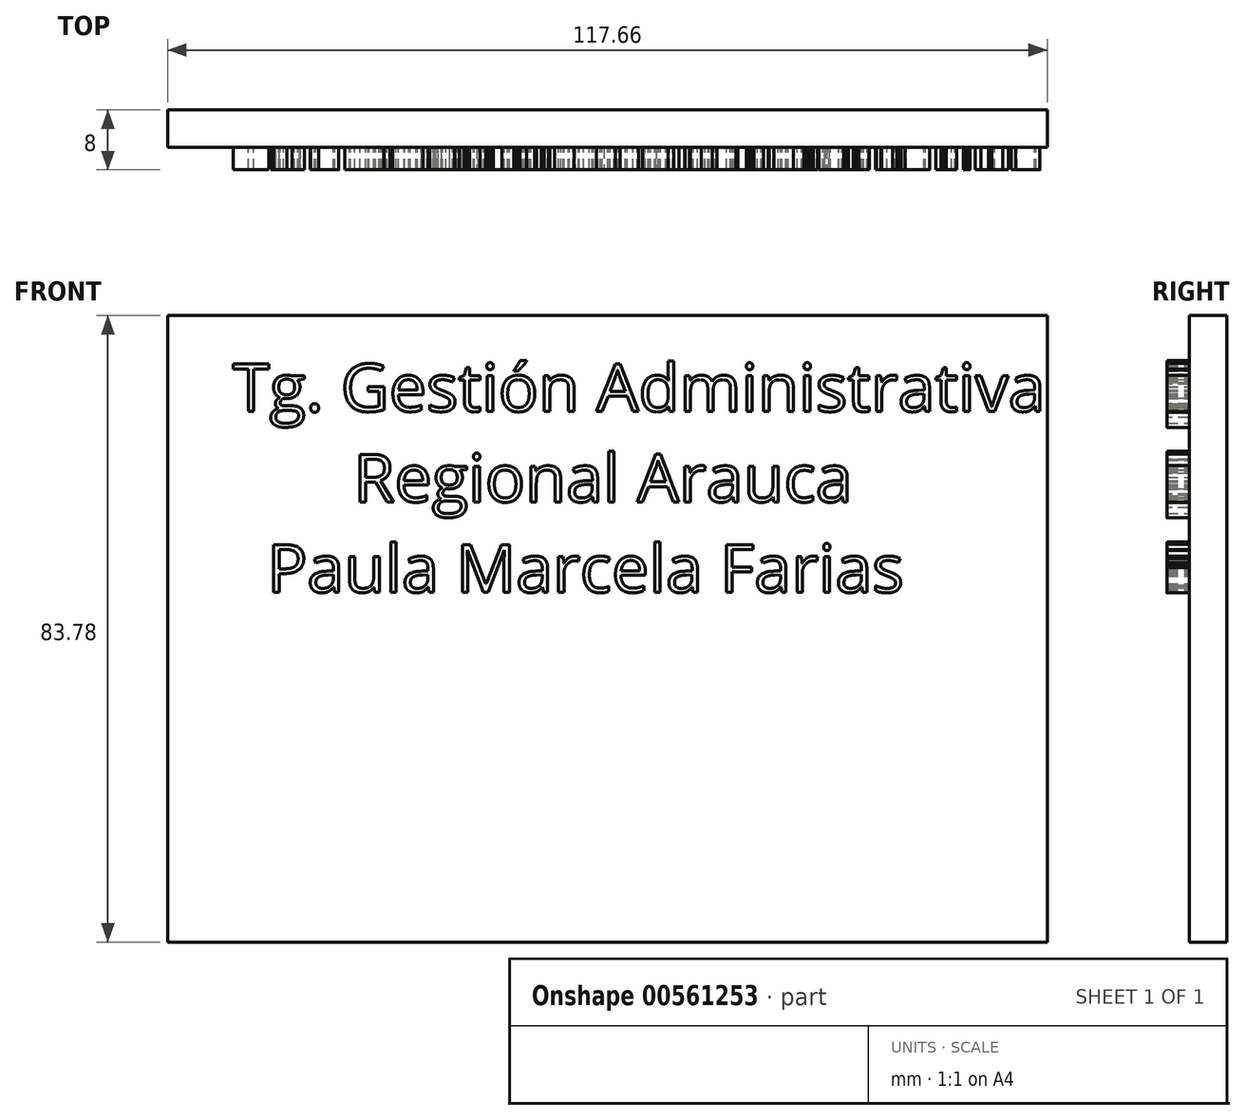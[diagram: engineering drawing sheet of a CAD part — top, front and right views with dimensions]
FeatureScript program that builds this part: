
annotation { "Feature Type Name" : "Feature", "Feature Type Description" : "" }
export const myFeature = defineFeature(function(context is Context, id is Id, definition is map)
    precondition{}
    {
        {
            var Q0;
            Q0=qCreatedBy(makeId("Front.planeOp"),FACE);
            var sketch = newSketch(context, id + "F0", { "sketchPlane" : qUnion([Q0])});
            skLineSegment(sketch, "E0.bottom", {"start": v(58.83, 41.9) * mm, "end": v(-58.83, 41.9) * mm});
            skLineSegment(sketch, "E0.top", {"start": v(58.83, -41.9) * mm, "end": v(-58.83, -41.9) * mm});
            skLineSegment(sketch, "E0.left", {"start": v(58.83, 41.9) * mm, "end": v(58.83, -41.9) * mm});
            skLineSegment(sketch, "E0.right", {"start": v(-58.83, 41.9) * mm, "end": v(-58.83, -41.9) * mm});
            skPoint(sketch, "E0.middle", {"position": v(0, 0) * mm});
            skSolve(sketch);
        }
        {
            var Q0;
            Q0=makeQuery(id+"F0.imprint","IMPRINT",FACE,{"disambiguationData":[TD([[makeQuery(id+"F0.imprint","IMPRINT",EDGE,{"derivedFrom":sQuery(id+"F0.wireOp",EDGE,"E0.bottom")}),1.0]])]});
            extrude(context, id + "F1", {"entities" : qUnion([Q0]), "oppositeDirection" : true, "depth" : 5 * mm, "offsetDistance" : 25 * mm});
        }
        {
            var Q0;
            Q0=makeQuery(id+"F1.opExtrude","CAP_FACE",FACE,{"disambiguationData":[OSD([sQuery(id+"F0.wireOp",EDGE,"E0.bottom"),sQuery(id+"F0.wireOp",EDGE,"E0.top"),sQuery(id+"F0.wireOp",EDGE,"E0.left"),sQuery(id+"F0.wireOp",EDGE,"E0.right")])],"isStart":true});
            var sketch = newSketch(context, id + "F2", { "sketchPlane" : qUnion([Q0])});
            skText(sketch, "E1", { "text": "Tg. Gestión Administrativa\n       Regional Arauca\n  Paula Marcela Farias", "fontName": "OpenSans-Regular.ttf"});
            const initialGuessF2  = {"E1": [-0.05013, 0.02907, 1, 0, 0.0064]};
            skSetInitialGuess(sketch, initialGuessF2);
            skSolve(sketch);
        }
        {
            var Q0;
            Q0 = qSketchRegion(id + "F2", true);
            extrude(context, id + "F3", {"entities" : qUnion([Q0]), "operationType" : NewBodyOperationType.ADD, "depth" : 3 * mm, "offsetDistance" : 25 * mm});
        }
    });
